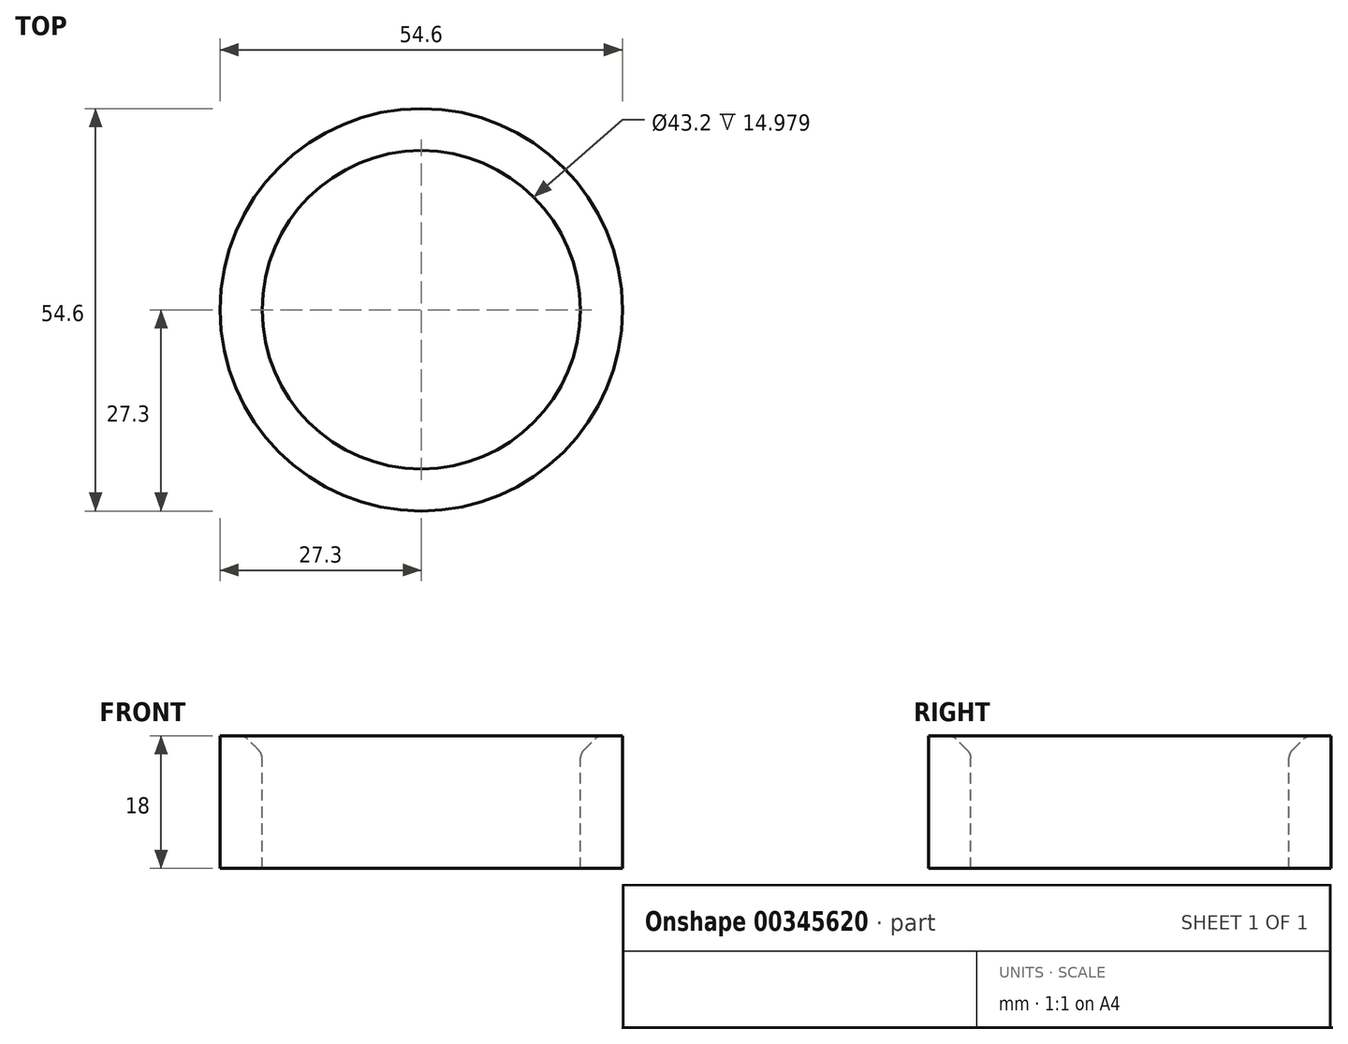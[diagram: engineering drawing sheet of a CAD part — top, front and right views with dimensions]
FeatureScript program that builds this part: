
annotation { "Feature Type Name" : "Feature", "Feature Type Description" : "" }
export const myFeature = defineFeature(function(context is Context, id is Id, definition is map)
    precondition{}
    {
        {
            var Q0;
            Q0=qCreatedBy(makeId("Front.planeOp"),FACE);
            var sketch = newSketch(context, id + "F0", { "sketchPlane" : qUnion([Q0])});
            skLineSegment(sketch, "E0", {"start": v(21.6, 0) * mm, "end": v(21.6, 15.6) * mm});
            skLineSegment(sketch, "E1", {"start": v(21.6, 15.6) * mm, "end": v(24, 18) * mm});
            skLineSegment(sketch, "E2", {"start": v(24, 18) * mm, "end": v(27.3, 18) * mm});
            skLineSegment(sketch, "E3", {"start": v(27.3, 18) * mm, "end": v(27.3, 0) * mm});
            skLineSegment(sketch, "E4", {"start": v(27.3, 0) * mm, "end": v(21.6, 0) * mm});
            skLineSegment(sketch, "E5", {"start": v(0, 34.5) * mm, "end": v(0, -24.78) * mm, "construction": true});
            skPoint(sketch, "E6.endSnap0", {"position": v(21.6, 7.8) * mm});
            skSolve(sketch);
        }
        {
            var Q0;
            Q0=makeQuery(id+"F0.imprint","IMPRINT",FACE,{"disambiguationData":[TD([[makeQuery(id+"F0.imprint","IMPRINT",EDGE,{"derivedFrom":sQuery(id+"F0.wireOp",EDGE,"E0")}),-1.0]])]});
            var Q1;
            Q1=sQuery(id+"F0.wireOp",EDGE,"E5");
            revolve(context, id + "F1", {"entities" : qUnion([Q0]), "axis" : qUnion([Q1]), "revolveType" : RevolveType.FULL});
        }
        {
            var Q0;
            Q0=makeQuery(id+"F1.opRevolve","SWEPT_EDGE",EDGE,{"disambiguationData":[OSD([sQuery(id+"F0.wireOp",EDGE,"E0"),sQuery(id+"F0.wireOp",EDGE,"E1")])]});
            fillet(context, id + "F2", {"entities" : qUnion([Q0]), "radius" : 1.5 * mm, "tangentPropagation" : true, "allowEdgeOverflow" : false});
        }
        {
            var Q0;
            Q0=makeQuery(id+"F1.opRevolve","SWEPT_EDGE",EDGE,{"disambiguationData":[OSD([sQuery(id+"F0.wireOp",EDGE,"E1"),sQuery(id+"F0.wireOp",EDGE,"E2")])]});
            fillet(context, id + "F3", {"entities" : qUnion([Q0]), "radius" : 1.5 * mm, "tangentPropagation" : true, "allowEdgeOverflow" : false});
        }
    });
